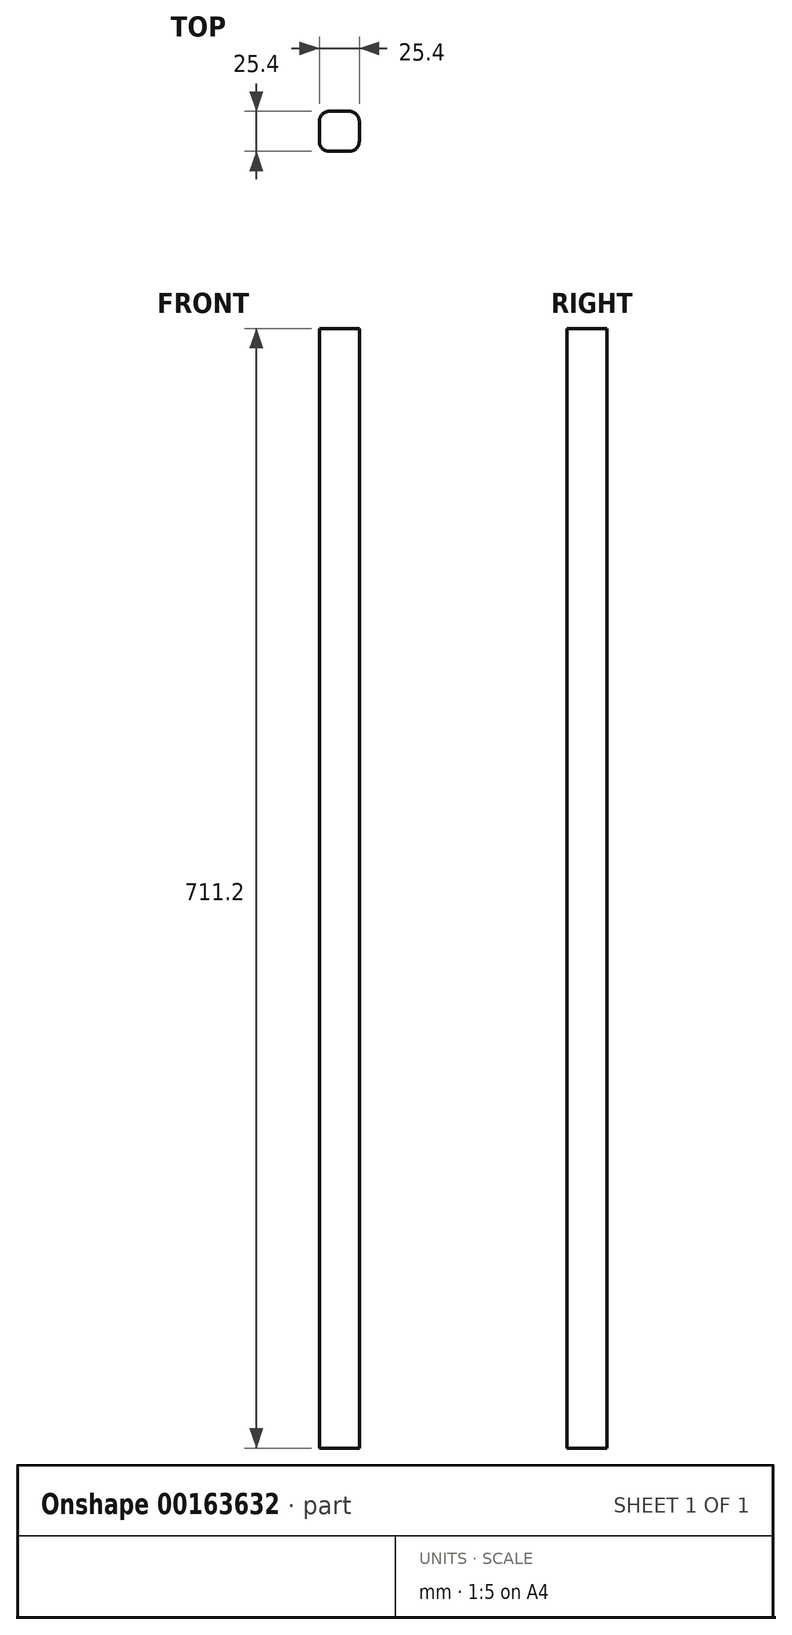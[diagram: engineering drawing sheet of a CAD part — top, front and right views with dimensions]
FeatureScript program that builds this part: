
annotation { "Feature Type Name" : "Feature", "Feature Type Description" : "" }
export const myFeature = defineFeature(function(context is Context, id is Id, definition is map)
    precondition{}
    {
        {
            var Q0;
            Q0=qCreatedBy(makeId("Top.planeOp"),FACE);
            var sketch = newSketch(context, id + "F0", { "sketchPlane" : qUnion([Q0])});
            skLineSegment(sketch, "E0.bottom", {"start": v(6.35, 12.7) * mm, "end": v(-6.35, 12.7) * mm});
            skLineSegment(sketch, "E0.top", {"start": v(6.35, -12.7) * mm, "end": v(-6.35, -12.7) * mm});
            skLineSegment(sketch, "E0.left", {"start": v(12.7, 6.35) * mm, "end": v(12.7, -6.35) * mm});
            skLineSegment(sketch, "E0.right", {"start": v(-12.7, 6.35) * mm, "end": v(-12.7, -6.35) * mm});
            skPoint(sketch, "E0.middle", {"position": v(0, 0) * mm});
            skPoint(sketch, "E1.visualSharp", {"position": v(-12.7, 12.7) * mm});
            skArc(sketch, "E1.filletArc", {"start": v(-6.35, 12.7) * mm, "mid": v(-10.84, 10.84) * mm, "end": v(-12.7, 6.35) * mm});
            skPoint(sketch, "E2.visualSharp", {"position": v(-12.7, -12.7) * mm});
            skArc(sketch, "E2.filletArc", {"start": v(-12.7, -6.35) * mm, "mid": v(-10.84, -10.84) * mm, "end": v(-6.35, -12.7) * mm});
            skPoint(sketch, "E3.visualSharp", {"position": v(12.7, -12.7) * mm});
            skArc(sketch, "E3.filletArc", {"start": v(6.35, -12.7) * mm, "mid": v(10.84, -10.84) * mm, "end": v(12.7, -6.35) * mm});
            skPoint(sketch, "E4.visualSharp", {"position": v(12.7, 12.7) * mm});
            skArc(sketch, "E4.filletArc", {"start": v(12.7, 6.35) * mm, "mid": v(10.84, 10.84) * mm, "end": v(6.35, 12.7) * mm});
            skSolve(sketch);
        }
        {
            var Q0;
            Q0=qSketchRegion(id+"F0",true);
            extrude(context, id + "F1", {"entities" : qUnion([Q0]), "depth" : 711.2 * mm, "offsetDistance" : 25.4 * mm});
        }
    });
